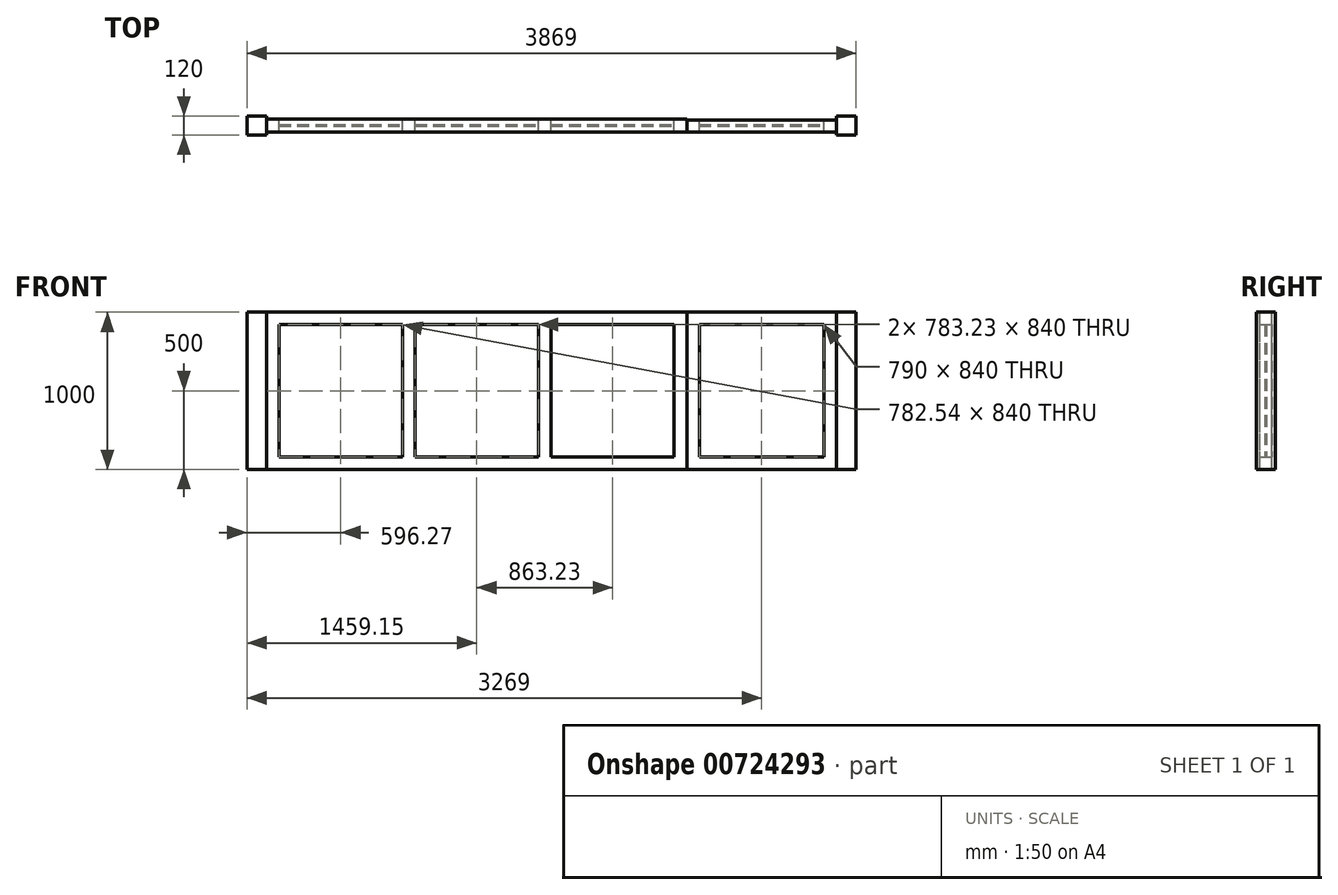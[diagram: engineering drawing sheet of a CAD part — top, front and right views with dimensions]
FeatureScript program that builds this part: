
annotation { "Feature Type Name" : "Feature", "Feature Type Description" : "" }
export const myFeature = defineFeature(function(context is Context, id is Id, definition is map)
    precondition{}
    {
        {
            var Q0;
            Q0=qCreatedBy(makeId("Front.planeOp"),FACE);
            var sketch = newSketch(context, id + "F0", { "sketchPlane" : qUnion([Q0])});
            skLineSegment(sketch, "E0.bottom", {"start": v(0, 0) * mm, "end": v(-1075, 0) * mm});
            skLineSegment(sketch, "E0.top", {"start": v(0, 1000) * mm, "end": v(-1075, 1000) * mm});
            skLineSegment(sketch, "E0.left", {"start": v(0, 0) * mm, "end": v(0, 1000) * mm});
            skLineSegment(sketch, "E0.right", {"start": v(-1075, 0) * mm, "end": v(-1075, 1000) * mm});
            skLineSegment(sketch, "E1.bottom", {"start": v(-1075, 0) * mm, "end": v(-3744, 0) * mm});
            skLineSegment(sketch, "E1.right", {"start": v(-3744, 0) * mm, "end": v(-3744, 1000) * mm});
            skLineSegment(sketch, "E2.bottom", {"start": v(-1075, 1000) * mm, "end": v(-3744, 1000) * mm});
            skLineSegment(sketch, "E2.left", {"start": v(-1075, 1000) * mm, "end": v(-1075, 0) * mm});
            skLineSegment(sketch, "E2.right", {"start": v(-3744, 1000) * mm, "end": v(-3744, 0) * mm});
            skLineSegment(sketch, "E3.bottom", {"start": v(-3664, 920) * mm, "end": v(-2881.46, 920) * mm});
            skLineSegment(sketch, "E3.top", {"start": v(-3664, 80) * mm, "end": v(-2881.46, 80) * mm});
            skLineSegment(sketch, "E3.left", {"start": v(-3664, 920) * mm, "end": v(-3664, 80) * mm});
            skLineSegment(sketch, "E3.right", {"start": v(-2881.46, 920) * mm, "end": v(-2881.46, 80) * mm});
            skLineSegment(sketch, "E4.bottom", {"start": v(-2801.46, 920) * mm, "end": v(-2018.23, 920) * mm});
            skLineSegment(sketch, "E4.top", {"start": v(-2801.46, 80) * mm, "end": v(-2018.23, 80) * mm});
            skLineSegment(sketch, "E4.left", {"start": v(-2801.46, 920) * mm, "end": v(-2801.46, 80) * mm});
            skLineSegment(sketch, "E4.right", {"start": v(-2018.23, 920) * mm, "end": v(-2018.23, 80) * mm});
            skLineSegment(sketch, "E5.bottom", {"start": v(-1938.23, 920) * mm, "end": v(-1155, 920) * mm});
            skLineSegment(sketch, "E5.top", {"start": v(-1938.23, 80) * mm, "end": v(-1155, 80) * mm});
            skLineSegment(sketch, "E5.left", {"start": v(-1938.23, 920) * mm, "end": v(-1938.23, 80) * mm});
            skLineSegment(sketch, "E5.right", {"start": v(-1155, 920) * mm, "end": v(-1155, 80) * mm});
            skLineSegment(sketch, "E6.bottom", {"start": v(-995, 920) * mm, "end": v(-205, 920) * mm});
            skLineSegment(sketch, "E6.top", {"start": v(-995, 80) * mm, "end": v(-205, 80) * mm});
            skLineSegment(sketch, "E6.left", {"start": v(-995, 920) * mm, "end": v(-995, 80) * mm});
            skLineSegment(sketch, "E6.right", {"start": v(-205, 920) * mm, "end": v(-205, 80) * mm});
            skLineSegment(sketch, "E7.bottom", {"start": v(0, 1000) * mm, "end": v(-125, 1000) * mm});
            skLineSegment(sketch, "E7.top", {"start": v(0, 0) * mm, "end": v(-125, 0) * mm});
            skLineSegment(sketch, "E7.left", {"start": v(0, 1000) * mm, "end": v(0, 0) * mm});
            skLineSegment(sketch, "E7.right", {"start": v(-125, 1000) * mm, "end": v(-125, 0) * mm});
            skLineSegment(sketch, "E8.bottom", {"start": v(-3744, 0) * mm, "end": v(-3869, 0) * mm});
            skLineSegment(sketch, "E8.right", {"start": v(-3869, 0) * mm, "end": v(-3869, 1000) * mm});
            skLineSegment(sketch, "E9", {"start": v(-3744, 1000) * mm, "end": v(-3869, 1000) * mm});
            skSolve(sketch);
        }
        {
            var Q0;
            Q0=makeQuery(id+"F0.imprint","IMPRINT",FACE,{"disambiguationData":[TD([[makeQuery(id+"F0.imprint","IMPRINT",EDGE,{"derivedFrom":sQuery(id+"F0.wireOp",EDGE,"E1.right")}),1.0]])]});
            var Q1;
            {var subQ2=sQuery(id+"F0.wireOp",EDGE,"E0.left");Q1=makeQuery(id+"F0.imprint","IMPRINT",FACE,{"disambiguationData":[TD([[makeQuery(id+"F0.imprint","IMPRINT",EDGE,{"derivedFrom":subQ2}),1.0]])]});}
            extrude(context, id + "F1", {"entities" : qUnion([Q0, Q1]), "depth" : 120 * mm, "offsetDistance" : 25 * mm});
        }
        {
            var Q0;
            Q0=makeQuery(id+"F0.imprint","IMPRINT",FACE,{"disambiguationData":[TD([[makeQuery(id+"F0.imprint","IMPRINT",EDGE,{"derivedFrom":sQuery(id+"F0.wireOp",EDGE,"E0.right")}),1.0]])]});
            extrude(context, id + "F2", {"entities" : qUnion([Q0]), "depth" : 100 * mm, "offsetDistance" : 25 * mm});
        }
        {
            var Q0;
            Q0=makeQuery(id+"F0.imprint","IMPRINT",FACE,{"disambiguationData":[TD([[makeQuery(id+"F0.imprint","IMPRINT",EDGE,{"derivedFrom":sQuery(id+"F0.wireOp",EDGE,"E3.bottom")}),-1.0]])]});
            var Q1;
            Q1=makeQuery(id+"F0.imprint","IMPRINT",FACE,{"disambiguationData":[TD([[makeQuery(id+"F0.imprint","IMPRINT",EDGE,{"derivedFrom":sQuery(id+"F0.wireOp",EDGE,"E4.bottom")}),-1.0]])]});
            var Q2;
            Q2=makeQuery(id+"F0.imprint","IMPRINT",FACE,{"disambiguationData":[TD([[makeQuery(id+"F0.imprint","IMPRINT",EDGE,{"derivedFrom":sQuery(id+"F0.wireOp",EDGE,"E5.bottom")}),-1.0]])]});
            extrude(context, id + "F3", {"entities" : qUnion([Q0, Q1, Q2]), "depth" : 65 * mm, "offsetDistance" : 25 * mm});
        }
        {
            var Q0;
            {var subQ2=sQuery(id+"F0.wireOp",EDGE,"E0.right");Q0=makeQuery(id+"F0.imprint","IMPRINT",FACE,{"disambiguationData":[TD([[makeQuery(id+"F0.imprint","IMPRINT",EDGE,{"derivedFrom":subQ2}),-1.0]])]});}
            extrude(context, id + "F4", {"entities" : qUnion([Q0]), "depth" : 100 * mm, "offsetDistance" : 25 * mm});
        }
        {
            var Q0;
            Q0=makeQuery(id+"F0.imprint","IMPRINT",FACE,{"disambiguationData":[TD([[makeQuery(id+"F0.imprint","IMPRINT",EDGE,{"derivedFrom":sQuery(id+"F0.wireOp",EDGE,"E6.bottom")}),-1.0]])]});
            extrude(context, id + "F5", {"entities" : qUnion([Q0]), "depth" : 65 * mm, "offsetDistance" : 25 * mm});
        }
        {
            var Q0;
            {var subQ2=sQuery(id+"F0.wireOp",EDGE,"E0.right");Q0=makeQuery(id+"F0.imprint","IMPRINT",FACE,{"disambiguationData":[TD([[makeQuery(id+"F0.imprint","IMPRINT",EDGE,{"derivedFrom":subQ2}),-1.0]])]});}
            extrude(context, id + "F6", {"entities" : qUnion([Q0]), "operationType" : NewBodyOperationType.REMOVE, "depth" : 25 * mm, "offsetDistance" : 25 * mm});
        }
        {
            var Q0;
            Q0=makeQuery(id+"F0.imprint","IMPRINT",FACE,{"disambiguationData":[TD([[makeQuery(id+"F0.imprint","IMPRINT",EDGE,{"derivedFrom":sQuery(id+"F0.wireOp",EDGE,"E6.bottom")}),-1.0]])]});
            extrude(context, id + "F7", {"entities" : qUnion([Q0]), "operationType" : NewBodyOperationType.REMOVE, "depth" : 55 * mm, "offsetDistance" : 25 * mm});
        }
        {
            var Q0;
            Q0=makeQuery(id+"F0.imprint","IMPRINT",FACE,{"disambiguationData":[TD([[makeQuery(id+"F0.imprint","IMPRINT",EDGE,{"derivedFrom":sQuery(id+"F0.wireOp",EDGE,"E0.right")}),1.0]])]});
            extrude(context, id + "F8", {"entities" : qUnion([Q0]), "operationType" : NewBodyOperationType.REMOVE, "depth" : 20 * mm, "offsetDistance" : 25 * mm});
        }
        {
            var Q0;
            Q0=makeQuery(id+"F0.imprint","IMPRINT",FACE,{"disambiguationData":[TD([[makeQuery(id+"F0.imprint","IMPRINT",EDGE,{"derivedFrom":sQuery(id+"F0.wireOp",EDGE,"E5.bottom")}),-1.0]])]});
            var Q1;
            Q1=makeQuery(id+"F0.imprint","IMPRINT",FACE,{"disambiguationData":[TD([[makeQuery(id+"F0.imprint","IMPRINT",EDGE,{"derivedFrom":sQuery(id+"F0.wireOp",EDGE,"E4.bottom")}),-1.0]])]});
            var Q2;
            Q2=makeQuery(id+"F0.imprint","IMPRINT",FACE,{"disambiguationData":[TD([[makeQuery(id+"F0.imprint","IMPRINT",EDGE,{"derivedFrom":sQuery(id+"F0.wireOp",EDGE,"E3.bottom")}),-1.0]])]});
            extrude(context, id + "F9", {"entities" : qUnion([Q0, Q1, Q2]), "operationType" : NewBodyOperationType.REMOVE, "depth" : 55 * mm, "offsetDistance" : 25 * mm});
        }
    });
